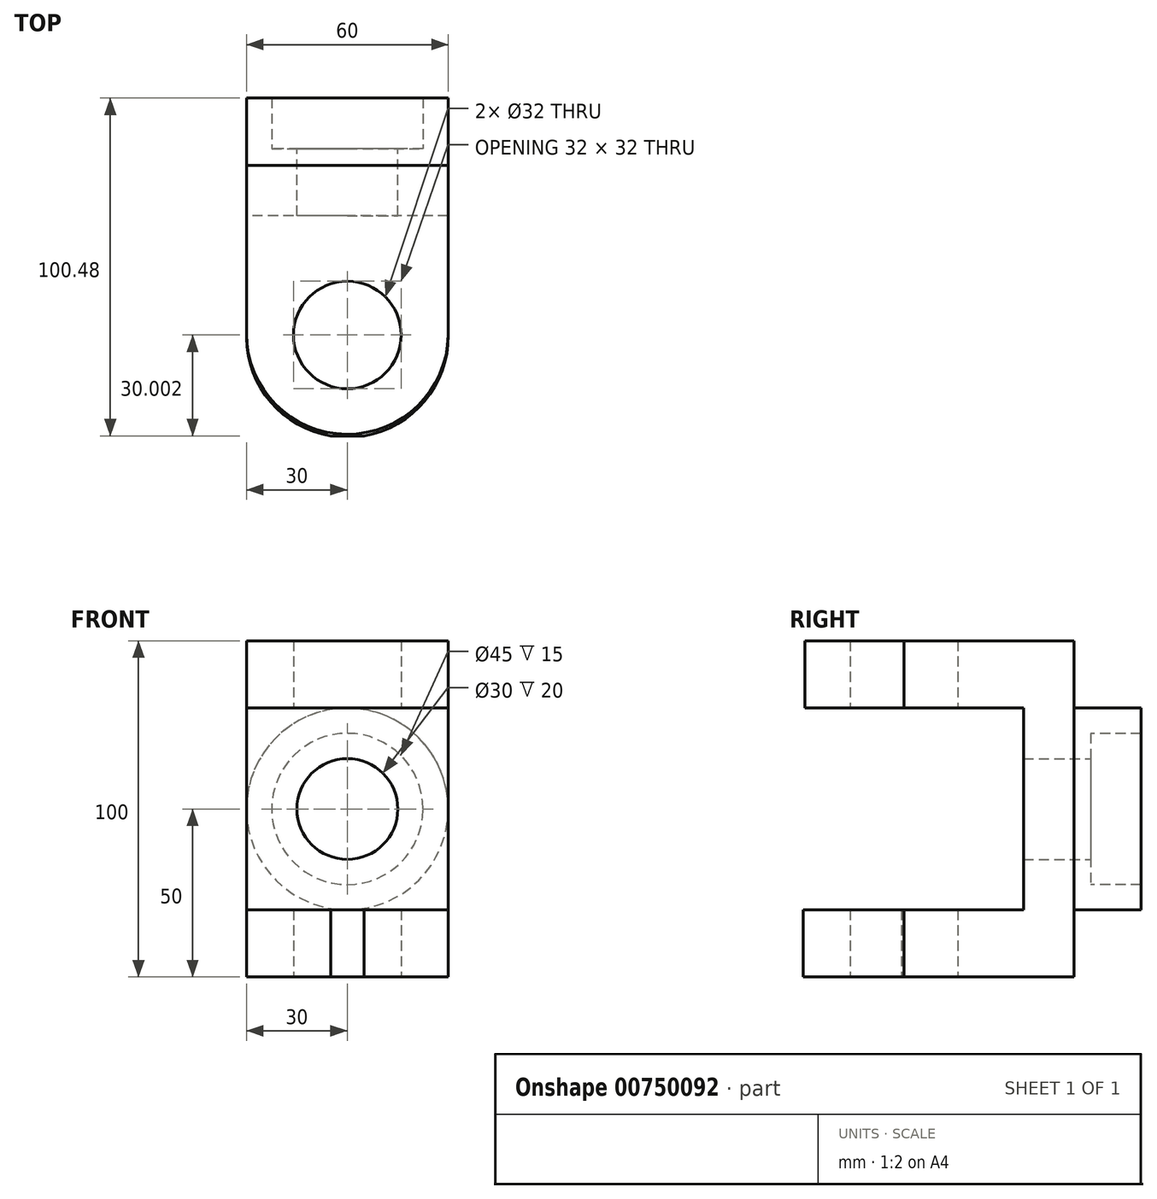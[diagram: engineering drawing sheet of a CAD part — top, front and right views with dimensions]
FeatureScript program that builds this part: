
annotation { "Feature Type Name" : "Feature", "Feature Type Description" : "" }
export const myFeature = defineFeature(function(context is Context, id is Id, definition is map)
    precondition{}
    {
        {
            var Q0;
            Q0=qCreatedBy(makeId("Top.planeOp"),FACE);
            var sketch = newSketch(context, id + "F0", { "sketchPlane" : qUnion([Q0])});
            skLineSegment(sketch, "E0", {"start": v(0, 0) * mm, "end": v(-30, 0) * mm});
            skLineSegment(sketch, "E1", {"start": v(0, 0) * mm, "end": v(30, 0) * mm});
            skLineSegment(sketch, "E2", {"start": v(-30, 0) * mm, "end": v(-30, -50.48) * mm});
            skLineSegment(sketch, "E3.MirrorCS", {"start": v(30, 0) * mm, "end": v(30, -50.48) * mm});
            skPoint(sketch, "E4", {"position": v(0, -50.48) * mm});
            skCircle(sketch, "E5", {"center": v(0, -50.48) * mm, "radius": 16 * mm});
            skLineSegment(sketch, "E6", {"start": v(-30, -50.48) * mm, "end": v(-30, -80.48) * mm});
            skLineSegment(sketch, "E7", {"start": v(-30, -80.48) * mm, "end": v(30.41, -80.48) * mm});
            skLineSegment(sketch, "E8", {"start": v(30, -50.48) * mm, "end": v(30.41, -80.48) * mm});
            skSolve(sketch);
        }
        {
            var Q0;
            Q0=makeQuery(id+"F0.imprint","IMPRINT",FACE,{"disambiguationData":[TD([[makeQuery(id+"F0.imprint","IMPRINT",EDGE,{"derivedFrom":sQuery(id+"F0.wireOp",EDGE,"E0")}),1.0]])]});
            extrude(context, id + "F1", {"entities" : qUnion([Q0]), "depth" : 100 * mm, "offsetDistance" : 25 * mm});
        }
        {
            var Q0;
            Q0=makeQuery(id+"F1.opExtrude","SWEPT_FACE",FACE,{"disambiguationData":[OSD([sQuery(id+"F0.wireOp",EDGE,"E2"),sQuery(id+"F0.wireOp",EDGE,"E6")])]});
            var sketch = newSketch(context, id + "F2", { "sketchPlane" : qUnion([Q0])});
            skLineSegment(sketch, "E9", {"start": v(15, 20) * mm, "end": v(80.48, 20) * mm});
            skLineSegment(sketch, "E10", {"start": v(15, 80) * mm, "end": v(80.48, 80) * mm});
            skLineSegment(sketch, "E11", {"start": v(15, 20) * mm, "end": v(15, 80) * mm});
            skPoint(sketch, "E12.orphan", {"position": v(0, 20) * mm});
            skPoint(sketch, "E13.orphan", {"position": v(0, 80) * mm});
            skPoint(sketch, "E14.orphan", {"position": v(15, 100) * mm});
            skSolve(sketch);
        }
        {
            var Q0;
            {var subQ0=sQuery(id+"F2.wireOp",EDGE,"E9");Q0=makeQuery(id+"F2.imprint","IMPRINT",FACE,{"disambiguationData":[TD([[makeQuery(id+"F2.imprint","IMPRINT",EDGE,{"derivedFrom":subQ0}),1.0]])]});}
            extrude(context, id + "F3", {"entities" : qUnion([Q0]), "operationType" : NewBodyOperationType.REMOVE, "oppositeDirection" : true, "depth" : 60 * mm, "offsetDistance" : 25 * mm});
        }
        {
            var Q0;
            Q0=makeQuery(id+"F1.opExtrude","SWEPT_FACE",FACE,{"disambiguationData":[OSD([sQuery(id+"F0.wireOp",EDGE,"E8")])]});
            var sketch = newSketch(context, id + "F4", { "sketchPlane" : qUnion([Q0])});
            skLineSegment(sketch, "E15", {"start": v(-50.88, 80) * mm, "end": v(-80.89, 80) * mm});
            skLineSegment(sketch, "E16", {"start": v(-50.88, 20) * mm, "end": v(-80.89, 20) * mm});
            skSolve(sketch);
        }
        {
            var Q0;
            {var subQ0=sQuery(id+"F4.wireOp",EDGE,"E15");Q0=makeQuery(id+"F4.imprint","IMPRINT",FACE,{"disambiguationData":[TD([[makeQuery(id+"F4.imprint","IMPRINT",EDGE,{"derivedFrom":subQ0}),1.0]])]});}
            extrude(context, id + "F5", {"entities" : qUnion([Q0]), "operationType" : NewBodyOperationType.REMOVE, "oppositeDirection" : true, "depth" : 25 * mm, "offsetDistance" : 25 * mm});
        }
        {
            var Q0;
            Q0=makeQuery(id+"F1.opExtrude","CAP_FACE",FACE,{"disambiguationData":[OSD([sQuery(id+"F0.wireOp",EDGE,"E0"),sQuery(id+"F0.wireOp",EDGE,"E1"),sQuery(id+"F0.wireOp",EDGE,"E2"),sQuery(id+"F0.wireOp",EDGE,"E3.MirrorCS"),sQuery(id+"F0.wireOp",EDGE,"E5"),sQuery(id+"F0.wireOp",EDGE,"E6"),sQuery(id+"F0.wireOp",EDGE,"E7"),sQuery(id+"F0.wireOp",EDGE,"E8")])],"isStart":false});
            var sketch = newSketch(context, id + "F6", { "sketchPlane" : qUnion([Q0])});
            skPoint(sketch, "E17", {"position": v(-30, 0) * mm});
            skPoint(sketch, "E18", {"position": v(-30, -50) * mm});
            skPoint(sketch, "E19", {"position": v(30, -50) * mm});
            skLineSegment(sketch, "E20", {"start": v(0, -80.48) * mm, "end": v(0, -80) * mm});
            skPoint(sketch, "E21", {"position": v(0, -50) * mm});
            skArc(sketch, "E22", {"start": v(-30, -50) * mm, "mid": v(-0.24, -80) * mm, "end": v(30, -50.48) * mm});
            skSolve(sketch);
        }
        {
            var Q0;
            {var subQ0=sQuery(id+"F6.wireOp",EDGE,"E20");Q0=makeQuery(id+"F6.imprint","IMPRINT",FACE,{"disambiguationData":[TD([[makeQuery(id+"F6.imprint","IMPRINT",EDGE,{"derivedFrom":subQ0}),-1.0]])]});}
            var Q1;
            {var subQ0=sQuery(id+"F6.wireOp",EDGE,"E20");Q1=makeQuery(id+"F6.imprint","IMPRINT",FACE,{"disambiguationData":[TD([[makeQuery(id+"F6.imprint","IMPRINT",EDGE,{"derivedFrom":subQ0}),1.0]])]});}
            extrude(context, id + "F7", {"entities" : qUnion([Q0, Q1]), "operationType" : NewBodyOperationType.REMOVE, "oppositeDirection" : true, "depth" : 20 * mm, "offsetDistance" : 25 * mm});
        }
        {
            var Q0;
            Q0=makeQuery(id+"F1.opExtrude","CAP_FACE",FACE,{"disambiguationData":[OSD([sQuery(id+"F0.wireOp",EDGE,"E0"),sQuery(id+"F0.wireOp",EDGE,"E1"),sQuery(id+"F0.wireOp",EDGE,"E2"),sQuery(id+"F0.wireOp",EDGE,"E3.MirrorCS"),sQuery(id+"F0.wireOp",EDGE,"E5"),sQuery(id+"F0.wireOp",EDGE,"E6"),sQuery(id+"F0.wireOp",EDGE,"E7"),sQuery(id+"F0.wireOp",EDGE,"E8")])],"isStart":true});
            var sketch = newSketch(context, id + "F8", { "sketchPlane" : qUnion([Q0])});
            skLineSegment(sketch, "E23", {"start": v(30, 50.48) * mm, "end": v(30, 50.48) * mm});
            skPoint(sketch, "E24", {"position": v(30, 50.48) * mm});
            skPoint(sketch, "E25", {"position": v(-30, 51.3) * mm});
            skPoint(sketch, "E26", {"position": v(0, 50.89) * mm});
            skArc(sketch, "E27", {"start": v(30, 50.48) * mm, "mid": v(0.41, 80.89) * mm, "end": v(-30, 51.3) * mm});
            skLineSegment(sketch, "E28.trimOffspring", {"start": v(-30, 51.3) * mm, "end": v(-30, 51.3) * mm});
            skSolve(sketch);
        }
        {
            var Q0;
            {var subQ0=sQuery(id+"F8.wireOp",EDGE,"E28.trimOffspring");Q0=makeQuery(id+"F8.imprint","IMPRINT",FACE,{"disambiguationData":[TD([[makeQuery(id+"F8.imprint","IMPRINT",EDGE,{"derivedFrom":subQ0}),-1.0]])]});}
            var Q1;
            {var subQ0=sQuery(id+"F8.wireOp",EDGE,"E23");Q1=makeQuery(id+"F8.imprint","IMPRINT",FACE,{"disambiguationData":[TD([[makeQuery(id+"F8.imprint","IMPRINT",EDGE,{"derivedFrom":subQ0}),-1.0]])]});}
            extrude(context, id + "F9", {"entities" : qUnion([Q0, Q1]), "operationType" : NewBodyOperationType.REMOVE, "oppositeDirection" : true, "depth" : 20 * mm, "offsetDistance" : 25 * mm});
        }
        {
            var Q0;
            Q0=makeQuery(id+"F1.opExtrude","SWEPT_FACE",FACE,{"disambiguationData":[OSD([sQuery(id+"F0.wireOp",EDGE,"E0"),sQuery(id+"F0.wireOp",EDGE,"E1")])]});
            var sketch = newSketch(context, id + "F10", { "sketchPlane" : qUnion([Q0])});
            skPoint(sketch, "E29", {"position": v(0, 50) * mm});
            skPoint(sketch, "E30.orphan", {"position": v(0, 0) * mm});
            skPoint(sketch, "E31.end.orphan", {"position": v(0, 100) * mm});
            skPoint(sketch, "E32.start.orphan", {"position": v(30, 50) * mm});
            skPoint(sketch, "E33", {"position": v(-30, 50) * mm});
            skCircle(sketch, "E34", {"center": v(0, 50) * mm, "radius": 30 * mm});
            skCircle(sketch, "E35", {"center": v(0, 50) * mm, "radius": 15 * mm});
            skCircle(sketch, "E36", {"center": v(0, 50) * mm, "radius": 22.5 * mm});
            skSolve(sketch);
        }
        {
            var Q0;
            Q0=makeQuery(id+"F10.imprint","IMPRINT",FACE,{"disambiguationData":[TD([[makeQuery(id+"F10.imprint","IMPRINT",EDGE,{"derivedFrom":sQuery(id+"F10.wireOp",EDGE,"E36")}),-1.0]])]});
            extrude(context, id + "F11", {"entities" : qUnion([Q0]), "operationType" : NewBodyOperationType.ADD, "depth" : 20 * mm, "offsetDistance" : 25 * mm});
        }
        {
            var Q0;
            Q0=makeQuery(id+"F11.boolean.opBoolean","SPLIT",FACE,{"disambiguationData":[TD([makeQuery(id+"F11.opExtrude","SWEPT_FACE",FACE,{"disambiguationData":[OSD([sQuery(id+"F10.wireOp",EDGE,"E36")])]})])],"derivedFrom":makeQuery(id+"F1.opExtrude","SWEPT_FACE",FACE,{"disambiguationData":[OSD([sQuery(id+"F0.wireOp",EDGE,"E0"),sQuery(id+"F0.wireOp",EDGE,"E1")])]})});
            var sketch = newSketch(context, id + "F12", { "sketchPlane" : qUnion([Q0])});
            skPoint(sketch, "E37", {"position": v(0, 50) * mm});
            skPoint(sketch, "E38.orphan", {"position": v(0, 27.5) * mm});
            skCircle(sketch, "E39", {"center": v(0, 50) * mm, "radius": 15 * mm});
            skSolve(sketch);
        }
        {
            var Q0;
            Q0=makeQuery(id+"F12.imprint","IMPRINT",FACE,{"disambiguationData":[TD([[makeQuery(id+"F12.imprint","IMPRINT",EDGE,{"derivedFrom":sQuery(id+"F12.wireOp",EDGE,"E39")}),1.0]])]});
            extrude(context, id + "F13", {"entities" : qUnion([Q0]), "operationType" : NewBodyOperationType.REMOVE, "oppositeDirection" : true, "depth" : 155 * mm, "offsetDistance" : 25 * mm});
        }
        {
            var Q0;
            Q0=makeQuery(id+"F11.boolean.opBoolean","SPLIT",FACE,{"disambiguationData":[TD([makeQuery(id+"F11.opExtrude","SWEPT_FACE",FACE,{"disambiguationData":[OSD([sQuery(id+"F10.wireOp",EDGE,"E36")])]})])],"derivedFrom":makeQuery(id+"F1.opExtrude","SWEPT_FACE",FACE,{"disambiguationData":[OSD([sQuery(id+"F0.wireOp",EDGE,"E0"),sQuery(id+"F0.wireOp",EDGE,"E1")])]})});
            extrude(context, id + "F14", {"entities" : qUnion([Q0]), "operationType" : NewBodyOperationType.ADD, "depth" : 5 * mm, "offsetDistance" : 25 * mm});
        }
    });
